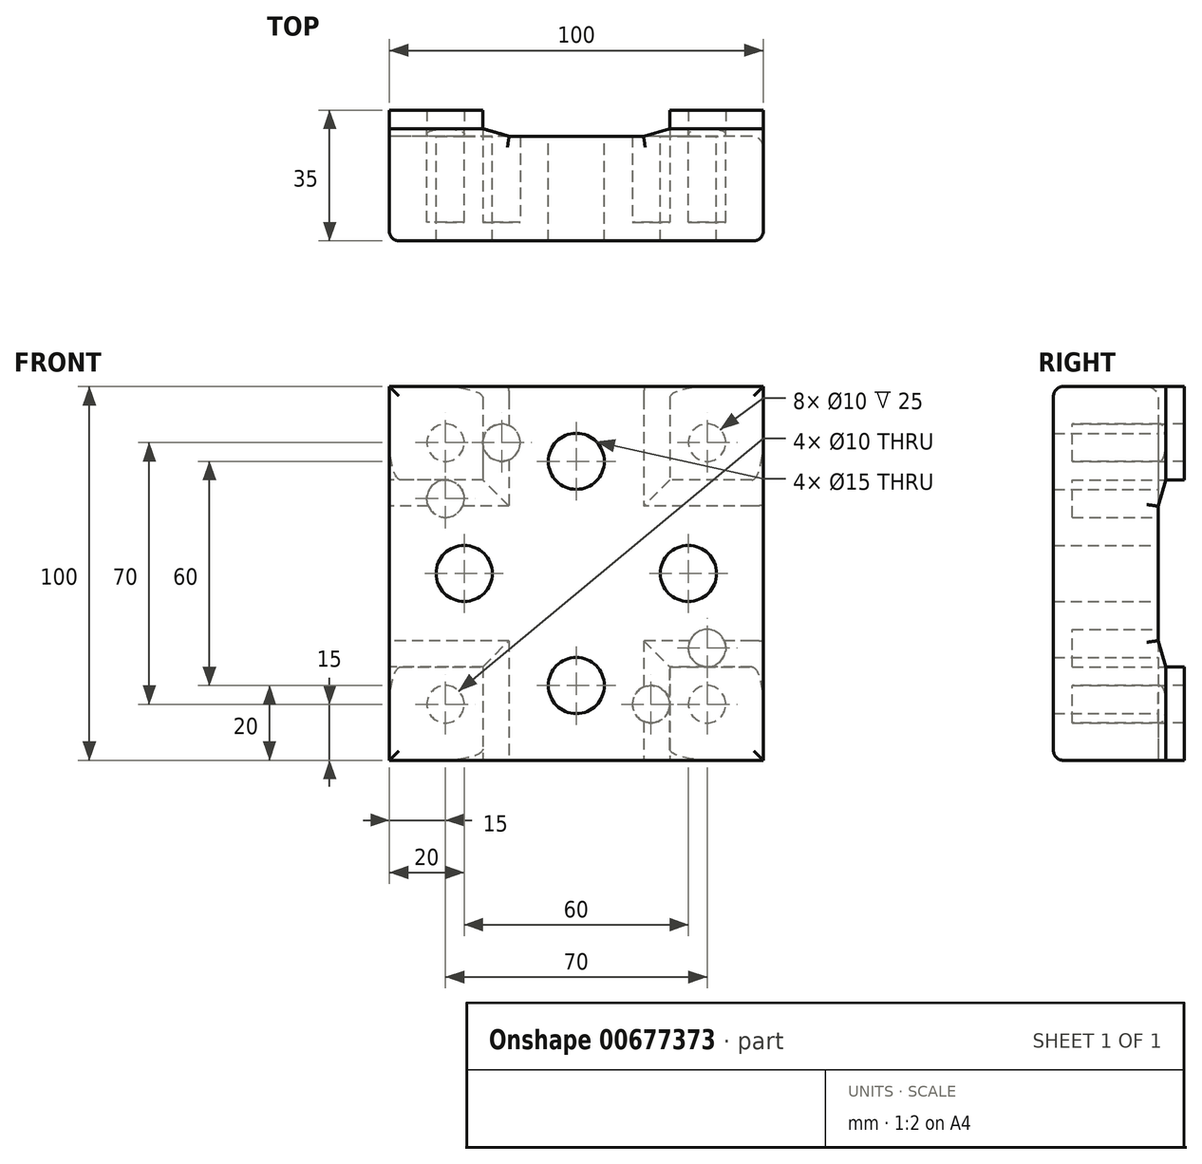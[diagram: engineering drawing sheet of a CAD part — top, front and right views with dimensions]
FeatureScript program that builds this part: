
annotation { "Feature Type Name" : "Feature", "Feature Type Description" : "" }
export const myFeature = defineFeature(function(context is Context, id is Id, definition is map)
    precondition{}
    {
        {
            var Q0;
            Q0=qCreatedBy(makeId("Front.planeOp"),FACE);
            var sketch = newSketch(context, id + "F0", { "sketchPlane" : qUnion([Q0])});
            skLineSegment(sketch, "E0.bottom", {"start": v(0, 0) * mm, "end": v(100, 0) * mm});
            skLineSegment(sketch, "E0.top", {"start": v(0, -100) * mm, "end": v(100, -100) * mm});
            skLineSegment(sketch, "E0.left", {"start": v(0, 0) * mm, "end": v(0, -100) * mm});
            skLineSegment(sketch, "E0.right", {"start": v(100, 0) * mm, "end": v(100, -100) * mm});
            skCircle(sketch, "E1", {"center": v(50, -20) * mm, "radius": 7.5 * mm});
            skCircle(sketch, "E2.1.0", {"center": v(20, -50) * mm, "radius": 7.5 * mm});
            skCircle(sketch, "E2.2.0", {"center": v(50, -80) * mm, "radius": 7.5 * mm});
            skCircle(sketch, "E2.3.0", {"center": v(80, -50) * mm, "radius": 7.5 * mm});
            skPoint(sketch, "E2.center", {"position": v(50, -50) * mm});
            skCircle(sketch, "E3", {"center": v(85, -15) * mm, "radius": 5 * mm});
            skCircle(sketch, "E4.1.0", {"center": v(15, -15) * mm, "radius": 5 * mm});
            skCircle(sketch, "E4.2.0", {"center": v(15, -85) * mm, "radius": 5 * mm});
            skCircle(sketch, "E4.3.0", {"center": v(85, -85) * mm, "radius": 5 * mm});
            skCircle(sketch, "E5", {"center": v(85, -70) * mm, "radius": 5 * mm});
            skCircle(sketch, "E6", {"center": v(15, -30) * mm, "radius": 5 * mm});
            skSolve(sketch);
        }
        {
            var Q0;
            Q0 = qSketchRegion(id + "F0", true);
            extrude(context, id + "F1", {"entities" : qUnion([Q0]), "depth" : 30 * mm, "offsetDistance" : 25 * mm});
        }
        {
            var Q0;
            Q0=makeQuery(id+"F1.opExtrude","SWEPT_FACE",FACE,{"disambiguationData":[OSD([sQuery(id+"F0.wireOp",EDGE,"E0.top")])]});
            var sketch = newSketch(context, id + "F2", { "sketchPlane" : qUnion([Q0])});
            skLineSegment(sketch, "E7", {"start": v(25, 0) * mm, "end": v(32, 2) * mm});
            skLineSegment(sketch, "E8", {"start": v(32, 2) * mm, "end": v(68, 2) * mm});
            skLineSegment(sketch, "E9", {"start": v(68, 2) * mm, "end": v(75, 0) * mm});
            skLineSegment(sketch, "E10", {"start": v(25, 0) * mm, "end": v(75, 0) * mm});
            skSolve(sketch);
        }
        {
            var Q0;
            Q0 = qSketchRegion(id + "F2", true);
            extrude(context, id + "F3", {"entities" : qUnion([Q0]), "operationType" : NewBodyOperationType.REMOVE, "endBound" : BoundingType.THROUGH_ALL, "oppositeDirection" : true, "depth" : 25 * mm, "offsetDistance" : 25 * mm});
        }
        {
            var Q0;
            Q0=makeQuery(id+"F1.opExtrude","SWEPT_FACE",FACE,{"disambiguationData":[OSD([sQuery(id+"F0.wireOp",EDGE,"E0.left")])]});
            var sketch = newSketch(context, id + "F4", { "sketchPlane" : qUnion([Q0])});
            skLineSegment(sketch, "E11", {"start": v(0, -25) * mm, "end": v(2, -32) * mm});
            skLineSegment(sketch, "E12", {"start": v(2, -32) * mm, "end": v(2, -68) * mm});
            skLineSegment(sketch, "E13", {"start": v(2, -68) * mm, "end": v(0, -75) * mm});
            skLineSegment(sketch, "E14", {"start": v(0, -25) * mm, "end": v(0, -75) * mm});
            skSolve(sketch);
        }
        {
            var Q0;
            Q0 = qSketchRegion(id + "F4", true);
            extrude(context, id + "F5", {"entities" : qUnion([Q0]), "operationType" : NewBodyOperationType.REMOVE, "endBound" : BoundingType.THROUGH_ALL, "oppositeDirection" : true, "depth" : 25 * mm, "offsetDistance" : 25 * mm});
        }
        {
            var Q0;
            Q0=makeQuery(id+"F1.opExtrude","CAP_EDGE",EDGE,{"disambiguationData":[OSD([sQuery(id+"F0.wireOp",EDGE,"E0.right")])],"isStart":false});
            var Q1;
            Q1=makeQuery(id+"F1.opExtrude","CAP_EDGE",EDGE,{"disambiguationData":[OSD([sQuery(id+"F0.wireOp",EDGE,"E0.bottom")])],"isStart":false});
            var Q2;
            Q2=makeQuery(id+"F1.opExtrude","CAP_EDGE",EDGE,{"disambiguationData":[OSD([sQuery(id+"F0.wireOp",EDGE,"E0.left")])],"isStart":false});
            var Q3;
            Q3=makeQuery(id+"F1.opExtrude","CAP_EDGE",EDGE,{"disambiguationData":[OSD([sQuery(id+"F0.wireOp",EDGE,"E0.top")])],"isStart":false});
            fillet(context, id + "F6", {"entities" : qUnion([Q0, Q1, Q2, Q3]), "radius" : 2.5 * mm, "tangentPropagation" : true, "allowEdgeOverflow" : false});
        }
        {
            var Q0;
            Q0=makeQuery(id+"F5.boolean.opBoolean","INTERSECT",EDGE,{"derivedFrom":[makeQuery(id+"F1.opExtrude","SWEPT_FACE",FACE,{"disambiguationData":[OSD([sQuery(id+"F0.wireOp",EDGE,"E0.right")])]}),makeQuery(id+"F5.opExtrude","SWEPT_FACE",FACE,{"disambiguationData":[OSD([sQuery(id+"F4.wireOp",EDGE,"E12")])]})]});
            var Q1;
            Q1=makeQuery(id+"F5.boolean.opBoolean","INTERSECT",EDGE,{"derivedFrom":[makeQuery(id+"F1.opExtrude","SWEPT_FACE",FACE,{"disambiguationData":[OSD([sQuery(id+"F0.wireOp",EDGE,"E0.right")])]}),makeQuery(id+"F5.opExtrude","SWEPT_FACE",FACE,{"disambiguationData":[OSD([sQuery(id+"F4.wireOp",EDGE,"E11")])]})]});
            var Q2;
            Q2=makeQuery(id+"F5.boolean.opBoolean","INTERSECT",EDGE,{"derivedFrom":[makeQuery(id+"F1.opExtrude","SWEPT_FACE",FACE,{"disambiguationData":[OSD([sQuery(id+"F0.wireOp",EDGE,"E0.right")])]}),makeQuery(id+"F5.opExtrude","SWEPT_FACE",FACE,{"disambiguationData":[OSD([sQuery(id+"F4.wireOp",EDGE,"E13")])]})]});
            var Q3;
            Q3=makeQuery(id+"F5.boolean.opBoolean","COPY",EDGE,{"derivedFrom":makeQuery(id+"F5.opExtrude","CAP_EDGE",EDGE,{"disambiguationData":[OSD([sQuery(id+"F4.wireOp",EDGE,"E12")])],"isStart":true})});
            var Q4;
            Q4=makeQuery(id+"F5.boolean.opBoolean","COPY",EDGE,{"derivedFrom":makeQuery(id+"F5.opExtrude","CAP_EDGE",EDGE,{"disambiguationData":[OSD([sQuery(id+"F4.wireOp",EDGE,"E13")])],"isStart":true})});
            var Q5;
            Q5=makeQuery(id+"F5.boolean.opBoolean","COPY",EDGE,{"derivedFrom":makeQuery(id+"F5.opExtrude","CAP_EDGE",EDGE,{"disambiguationData":[OSD([sQuery(id+"F4.wireOp",EDGE,"E11")])],"isStart":true})});
            var Q6;
            Q6=makeQuery(id+"F3.boolean.opBoolean","COPY",EDGE,{"derivedFrom":makeQuery(id+"F3.opExtrude","CAP_EDGE",EDGE,{"disambiguationData":[OSD([sQuery(id+"F2.wireOp",EDGE,"E8")])],"isStart":true})});
            var Q7;
            Q7=makeQuery(id+"F3.boolean.opBoolean","COPY",EDGE,{"derivedFrom":makeQuery(id+"F3.opExtrude","CAP_EDGE",EDGE,{"disambiguationData":[OSD([sQuery(id+"F2.wireOp",EDGE,"E9")])],"isStart":true})});
            var Q8;
            Q8=makeQuery(id+"F3.boolean.opBoolean","COPY",EDGE,{"derivedFrom":makeQuery(id+"F3.opExtrude","CAP_EDGE",EDGE,{"disambiguationData":[OSD([sQuery(id+"F2.wireOp",EDGE,"E7")])],"isStart":true})});
            var Q9;
            Q9=makeQuery(id+"F3.boolean.opBoolean","INTERSECT",EDGE,{"derivedFrom":[makeQuery(id+"F1.opExtrude","SWEPT_FACE",FACE,{"disambiguationData":[OSD([sQuery(id+"F0.wireOp",EDGE,"E0.bottom")])]}),makeQuery(id+"F3.opExtrude","SWEPT_FACE",FACE,{"disambiguationData":[OSD([sQuery(id+"F2.wireOp",EDGE,"E8")])]})]});
            var Q10;
            Q10=makeQuery(id+"F3.boolean.opBoolean","INTERSECT",EDGE,{"derivedFrom":[makeQuery(id+"F1.opExtrude","SWEPT_FACE",FACE,{"disambiguationData":[OSD([sQuery(id+"F0.wireOp",EDGE,"E0.bottom")])]}),makeQuery(id+"F3.opExtrude","SWEPT_FACE",FACE,{"disambiguationData":[OSD([sQuery(id+"F2.wireOp",EDGE,"E9")])]})]});
            var Q11;
            Q11=makeQuery(id+"F3.boolean.opBoolean","INTERSECT",EDGE,{"derivedFrom":[makeQuery(id+"F1.opExtrude","SWEPT_FACE",FACE,{"disambiguationData":[OSD([sQuery(id+"F0.wireOp",EDGE,"E0.bottom")])]}),makeQuery(id+"F3.opExtrude","SWEPT_FACE",FACE,{"disambiguationData":[OSD([sQuery(id+"F2.wireOp",EDGE,"E7")])]})]});
            fillet(context, id + "F7", {"entities" : qUnion([Q0, Q1, Q2, Q3, Q4, Q5, Q6, Q7, Q8, Q9, Q10, Q11]), "radius" : 3 * mm, "tangentPropagation" : true, "allowEdgeOverflow" : false});
        }
        {
            var Q0;
            {var subQ1=sQuery(id+"F0.wireOp",EDGE,"E3");var subQ3=sQuery(id+"F0.wireOp",EDGE,"E0.right");var subQ4=makeQuery(id+"F1.opExtrude","SWEPT_FACE",FACE,{"disambiguationData":[OSD([subQ3])]});var subQ5=sQuery(id+"F0.wireOp",EDGE,"E0.bottom");var subQ6=makeQuery(id+"F1.opExtrude","SWEPT_FACE",FACE,{"disambiguationData":[OSD([subQ5])]});var subQ7=sQuery(id+"F0.wireOp",EDGE,"E2.3.0");var subQ8=sQuery(id+"F0.wireOp",EDGE,"E0.top");var subQ9=sQuery(id+"F0.wireOp",EDGE,"E5");var subQ10=sQuery(id+"F0.wireOp",EDGE,"E4.3.0");Q0=makeQuery(id+"F5.boolean.opBoolean","SPLIT",FACE,{"disambiguationData":[TD([subQ6])],"derivedFrom":makeQuery(id+"F3.boolean.opBoolean","SPLIT",FACE,{"disambiguationData":[TD([subQ4])],"derivedFrom":makeQuery(id+"F1.opExtrude","CAP_FACE",FACE,{"disambiguationData":[OSD([subQ5,subQ8,sQuery(id+"F0.wireOp",EDGE,"E0.left"),subQ3,sQuery(id+"F0.wireOp",EDGE,"E1"),sQuery(id+"F0.wireOp",EDGE,"E2.1.0"),sQuery(id+"F0.wireOp",EDGE,"E2.2.0"),subQ7,subQ1,sQuery(id+"F0.wireOp",EDGE,"E4.1.0"),sQuery(id+"F0.wireOp",EDGE,"E4.2.0"),subQ10,subQ9,sQuery(id+"F0.wireOp",EDGE,"E6")])],"isStart":true})})});}
            var sketch = newSketch(context, id + "F8", { "sketchPlane" : qUnion([Q0])});
            skLineSegment(sketch, "E15.0.0", {"start": v(-100, 0) * mm, "end": v(-100, -14.08) * mm});
            skEllipticalArc(sketch, "E15.0.1", {});
            skLineSegment(sketch, "E15.0.2", {"start": v(-97, -25) * mm, "end": v(-75, -25) * mm});
            skLineSegment(sketch, "E15.0.3", {"start": v(-75, -25) * mm, "end": v(-75, -3) * mm});
            skEllipticalArc(sketch, "E15.0.4", {});
            skLineSegment(sketch, "E15.0.5", {"start": v(-85.92, 0) * mm, "end": v(-100, 0) * mm});
            skCircle(sketch, "E16.0", {"center": v(-85, -15) * mm, "radius": 5 * mm});
            skLineSegment(sketch, "E17.0.0", {"start": v(-15, -25) * mm, "end": v(-3, -25) * mm});
            skEllipticalArc(sketch, "E17.0.1", {});
            skLineSegment(sketch, "E17.0.2", {"start": v(0, -14.08) * mm, "end": v(0, 0) * mm});
            skLineSegment(sketch, "E17.0.3", {"start": v(0, 0) * mm, "end": v(-14.08, 0) * mm});
            skEllipticalArc(sketch, "E17.0.4", {});
            skLineSegment(sketch, "E17.0.5", {"start": v(-25, -3) * mm, "end": v(-25, -25) * mm});
            skLineSegment(sketch, "E17.0.6", {"start": v(-25, -25) * mm, "end": v(-15, -25) * mm});
            skCircle(sketch, "E18.0", {"center": v(-15, -15) * mm, "radius": 5 * mm});
            skLineSegment(sketch, "E19.0.0", {"start": v(0, -100) * mm, "end": v(0, -85.92) * mm});
            skEllipticalArc(sketch, "E19.0.1", {});
            skLineSegment(sketch, "E19.0.2", {"start": v(-3, -75) * mm, "end": v(-25, -75) * mm});
            skLineSegment(sketch, "E19.0.3", {"start": v(-25, -75) * mm, "end": v(-25, -97) * mm});
            skEllipticalArc(sketch, "E19.0.4", {});
            skLineSegment(sketch, "E19.0.5", {"start": v(-14.08, -100) * mm, "end": v(0, -100) * mm});
            skCircle(sketch, "E20.0", {"center": v(-15, -85) * mm, "radius": 5 * mm});
            skLineSegment(sketch, "E21.0.0", {"start": v(-85, -75) * mm, "end": v(-97, -75) * mm});
            skEllipticalArc(sketch, "E21.0.1", {});
            skLineSegment(sketch, "E21.0.2", {"start": v(-100, -85.92) * mm, "end": v(-100, -100) * mm});
            skLineSegment(sketch, "E21.0.3", {"start": v(-100, -100) * mm, "end": v(-85.92, -100) * mm});
            skEllipticalArc(sketch, "E21.0.4", {});
            skLineSegment(sketch, "E21.0.5", {"start": v(-75, -97) * mm, "end": v(-75, -75) * mm});
            skLineSegment(sketch, "E21.0.6", {"start": v(-75, -75) * mm, "end": v(-85, -75) * mm});
            skCircle(sketch, "E22.0", {"center": v(-85, -85) * mm, "radius": 5 * mm});
            const initialGuessF8  = {"E15.0.1": [-0.097, -0.014079835166079229, 0, 1, 0.010920164833920783, 0.003, 1.5707963267948966, 3.141592653589793], "E15.0.4": [-0.08592016483392081, -0.003, 1, 0, 0.010920164833920783, 0.003, 0, 1.5707963267948966], "E17.0.1": [-0.003, -0.014079835166079236, 0, 1, 0.010920164833920783, 0.003, 3.141592653589793, 4.71238898038469], "E17.0.4": [-0.014079835166079243, -0.003, 1, 0, 0.010920164833920765, 0.003, 1.5707963267948966, 3.141592653589793], "E19.0.1": [-0.003, -0.08592016483392084, 0, 1, 0.010920164833920795, 0.003, 4.71238898038469, 0], "E19.0.4": [-0.014079835166079243, -0.097, 1, 0, 0.010920164833920765, 0.003, 3.141592653589793, 4.71238898038469], "E21.0.1": [-0.097, -0.08592016483392084, 0, 1, 0.010920164833920795, 0.003, 0, 1.5707963267948966], "E21.0.4": [-0.08592016483392081, -0.097, 1, 0, 0.010920164833920783, 0.003, 4.71238898038469, 0]};
            skSetInitialGuess(sketch, initialGuessF8);
            skSolve(sketch);
        }
        {
            var Q0;
            Q0 = qSketchRegion(id + "F8", true);
            extrude(context, id + "F9", {"entities" : qUnion([Q0]), "depth" : 5 * mm, "offsetDistance" : 25 * mm});
        }
        {
            var Q0;
            Q0=makeQuery(id+"F1.opExtrude","CAP_FACE",FACE,{"disambiguationData":[OSD([sQuery(id+"F0.wireOp",EDGE,"E0.bottom"),sQuery(id+"F0.wireOp",EDGE,"E0.top"),sQuery(id+"F0.wireOp",EDGE,"E0.left"),sQuery(id+"F0.wireOp",EDGE,"E0.right"),sQuery(id+"F0.wireOp",EDGE,"E1"),sQuery(id+"F0.wireOp",EDGE,"E2.1.0"),sQuery(id+"F0.wireOp",EDGE,"E2.2.0"),sQuery(id+"F0.wireOp",EDGE,"E2.3.0"),sQuery(id+"F0.wireOp",EDGE,"E3"),sQuery(id+"F0.wireOp",EDGE,"E4.1.0"),sQuery(id+"F0.wireOp",EDGE,"E4.2.0"),sQuery(id+"F0.wireOp",EDGE,"E4.3.0"),sQuery(id+"F0.wireOp",EDGE,"E5"),sQuery(id+"F0.wireOp",EDGE,"E6")])],"isStart":false});
            var sketch = newSketch(context, id + "F10", { "sketchPlane" : qUnion([Q0])});
            skCircle(sketch, "E23.0", {"center": v(85, -85) * mm, "radius": 5 * mm});
            skCircle(sketch, "E24.0", {"center": v(15, -85) * mm, "radius": 5 * mm});
            skCircle(sketch, "E25.0", {"center": v(15, -15) * mm, "radius": 5 * mm});
            skCircle(sketch, "E26.0", {"center": v(85, -15) * mm, "radius": 5 * mm});
            skCircle(sketch, "E27", {"center": v(30, -15) * mm, "radius": 5 * mm});
            skCircle(sketch, "E28", {"center": v(70, -85) * mm, "radius": 5 * mm});
            skCircle(sketch, "E29.0", {"center": v(85, -70) * mm, "radius": 5 * mm});
            skCircle(sketch, "E30.0", {"center": v(15, -30) * mm, "radius": 5 * mm});
            skSolve(sketch);
        }
        {
            var Q0;
            Q0=makeQuery(id+"F10.imprint","IMPRINT",FACE,{"disambiguationData":[TD([[makeQuery(id+"F10.imprint","IMPRINT",EDGE,{"derivedFrom":sQuery(id+"F10.wireOp",EDGE,"E27")}),1.0]])]});
            var Q1;
            Q1=makeQuery(id+"F10.imprint","IMPRINT",FACE,{"disambiguationData":[TD([[makeQuery(id+"F10.imprint","IMPRINT",EDGE,{"derivedFrom":sQuery(id+"F10.wireOp",EDGE,"E28")}),1.0]])]});
            extrude(context, id + "F11", {"entities" : qUnion([Q0, Q1]), "operationType" : NewBodyOperationType.REMOVE, "endBound" : BoundingType.THROUGH_ALL, "oppositeDirection" : true, "depth" : 25 * mm, "offsetDistance" : 25 * mm});
        }
        {
            var Q0;
            Q0 = qSketchRegion(id + "F10", true);
            extrude(context, id + "F12", {"entities" : qUnion([Q0]), "operationType" : NewBodyOperationType.ADD, "oppositeDirection" : true, "depth" : 5 * mm, "offsetDistance" : 25 * mm});
        }
    });
